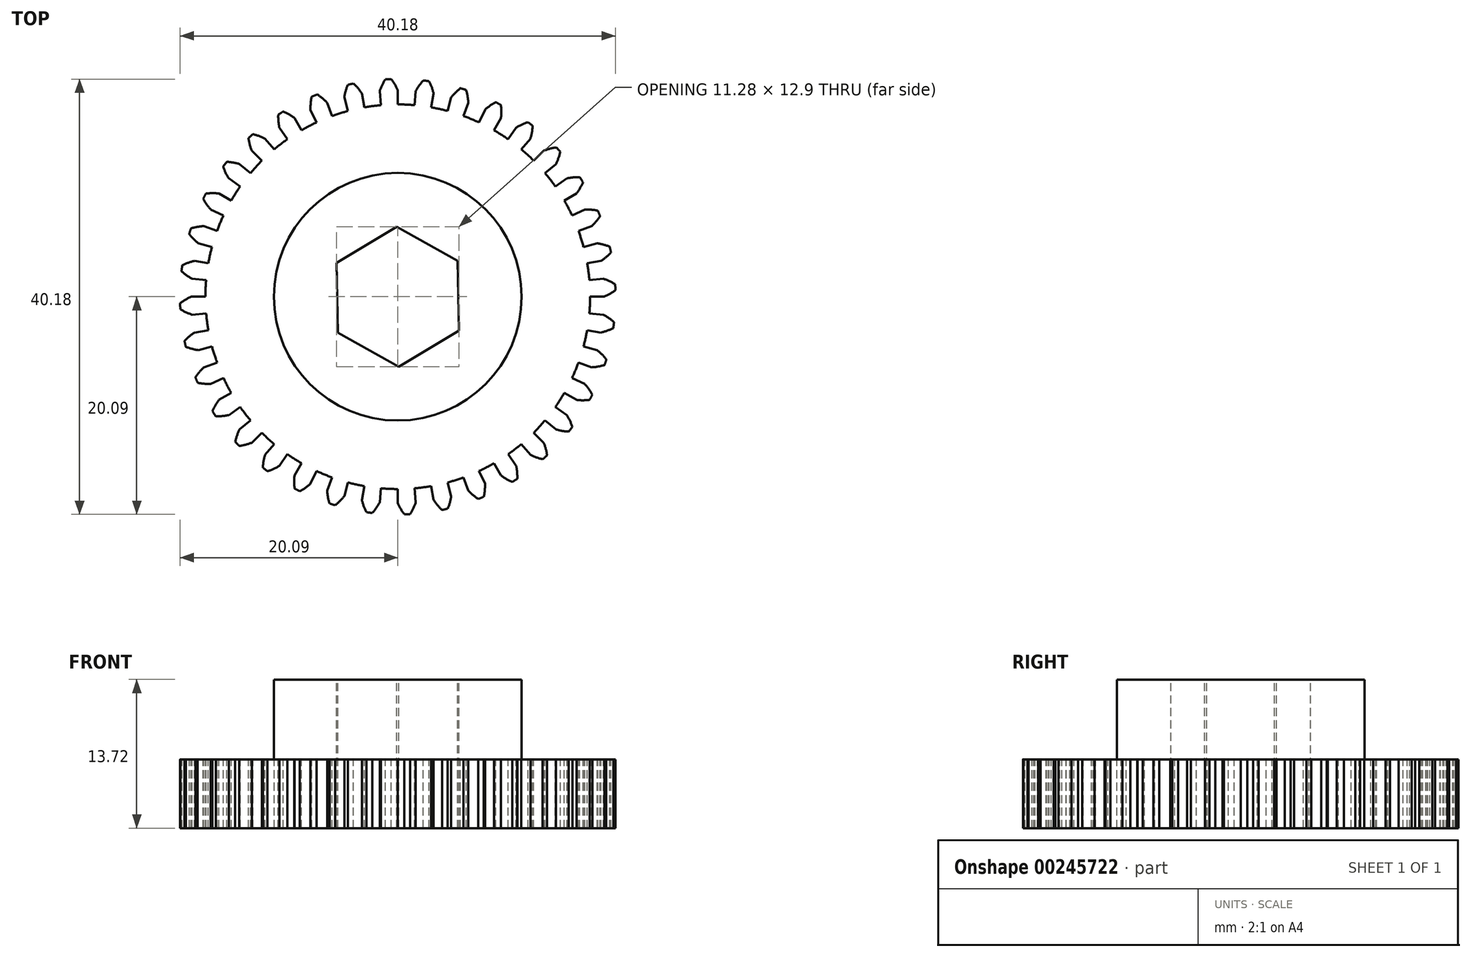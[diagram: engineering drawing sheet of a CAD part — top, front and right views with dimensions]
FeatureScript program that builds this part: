
annotation { "Feature Type Name" : "Feature", "Feature Type Description" : "" }
export const myFeature = defineFeature(function(context is Context, id is Id, definition is map)
    precondition{}
    {
        {
            var Q0;
            Q0=qCreatedBy(makeId("Top.planeOp"),FACE);
            var sketch = newSketch(context, id + "F0", { "sketchPlane" : qUnion([Q0])});
            skArc(sketch, "E0", {"start": v(-0.6, 20.1) * mm, "mid": v(-0.74, 20.1) * mm, "end": v(-0.88, 20.08) * mm});
            skLineSegment(sketch, "E1", {"start": v(0, 17.75) * mm, "end": v(0, 19.05) * mm});
            skLineSegment(sketch, "E2", {"start": v(-1.55, 17.69) * mm, "end": v(-1.66, 18.98) * mm});
            skArc(sketch, "E3", {"start": v(-4.6, 17.15) * mm, "mid": v(-5.34, 16.93) * mm, "end": v(-6.07, 16.68) * mm});
            skArc(sketch, "E4", {"start": v(0, 19.05) * mm, "mid": v(-0.27, 19.6) * mm, "end": v(-0.6, 20.1) * mm});
            skArc(sketch, "E5.MirrorCS", {"start": v(-1.66, 18.98) * mm, "mid": v(-1.44, 19.54) * mm, "end": v(-1.15, 20.07) * mm});
            skArc(sketch, "E6.MirrorCS", {"start": v(-1.15, 20.07) * mm, "mid": v(-1.01, 20.08) * mm, "end": v(-0.88, 20.08) * mm});
            skLineSegment(sketch, "E7.1.0", {"start": v(-4.6, 17.15) * mm, "end": v(-4.93, 18.4) * mm});
            skArc(sketch, "E7.1.1", {"start": v(-4.93, 18.4) * mm, "mid": v(-4.81, 19) * mm, "end": v(-4.62, 19.57) * mm});
            skArc(sketch, "E7.1.2", {"start": v(-4.62, 19.57) * mm, "mid": v(-4.48, 19.6) * mm, "end": v(-4.35, 19.63) * mm});
            skArc(sketch, "E7.1.3", {"start": v(-4.09, 19.68) * mm, "mid": v(-4.22, 19.66) * mm, "end": v(-4.35, 19.63) * mm});
            skArc(sketch, "E7.1.4", {"start": v(-3.3, 18.76) * mm, "mid": v(-3.67, 19.25) * mm, "end": v(-4.09, 19.68) * mm});
            skLineSegment(sketch, "E7.1.5", {"start": v(-3.08, 17.49) * mm, "end": v(-3.3, 18.76) * mm});
            skLineSegment(sketch, "E7.2.0", {"start": v(-7.5, 16.1) * mm, "end": v(-8.05, 17.27) * mm});
            skArc(sketch, "E7.2.1", {"start": v(-8.05, 17.27) * mm, "mid": v(-8.04, 17.87) * mm, "end": v(-7.94, 18.47) * mm});
            skArc(sketch, "E7.2.2", {"start": v(-7.94, 18.47) * mm, "mid": v(-7.82, 18.52) * mm, "end": v(-7.7, 18.57) * mm});
            skArc(sketch, "E7.2.3", {"start": v(-7.44, 18.68) * mm, "mid": v(-7.57, 18.63) * mm, "end": v(-7.7, 18.57) * mm});
            skArc(sketch, "E7.2.4", {"start": v(-6.52, 17.9) * mm, "mid": v(-6.95, 18.32) * mm, "end": v(-7.44, 18.68) * mm});
            skLineSegment(sketch, "E7.2.5", {"start": v(-6.07, 16.68) * mm, "end": v(-6.52, 17.9) * mm});
            skLineSegment(sketch, "E7.3.0", {"start": v(-10.18, 14.54) * mm, "end": v(-10.93, 15.6) * mm});
            skArc(sketch, "E7.3.1", {"start": v(-10.93, 15.6) * mm, "mid": v(-11.02, 16.2) * mm, "end": v(-11.03, 16.8) * mm});
            skArc(sketch, "E7.3.2", {"start": v(-11.03, 16.8) * mm, "mid": v(-10.92, 16.88) * mm, "end": v(-10.8, 16.96) * mm});
            skArc(sketch, "E7.3.3", {"start": v(-10.57, 17.1) * mm, "mid": v(-10.69, 17.03) * mm, "end": v(-10.8, 16.96) * mm});
            skArc(sketch, "E7.3.4", {"start": v(-9.53, 16.5) * mm, "mid": v(-10.03, 16.83) * mm, "end": v(-10.57, 17.1) * mm});
            skLineSegment(sketch, "E7.3.5", {"start": v(-8.88, 15.38) * mm, "end": v(-9.52, 16.5) * mm});
            skLineSegment(sketch, "E7.4.0", {"start": v(-12.55, 12.55) * mm, "end": v(-13.47, 13.47) * mm});
            skArc(sketch, "E7.4.1", {"start": v(-13.47, 13.47) * mm, "mid": v(-13.66, 14.04) * mm, "end": v(-13.78, 14.64) * mm});
            skArc(sketch, "E7.4.2", {"start": v(-13.78, 14.64) * mm, "mid": v(-13.68, 14.73) * mm, "end": v(-13.58, 14.82) * mm});
            skArc(sketch, "E7.4.3", {"start": v(-13.38, 15) * mm, "mid": v(-13.48, 14.91) * mm, "end": v(-13.58, 14.82) * mm});
            skArc(sketch, "E7.4.4", {"start": v(-12.25, 14.6) * mm, "mid": v(-12.8, 14.83) * mm, "end": v(-13.38, 15) * mm});
            skLineSegment(sketch, "E7.4.5", {"start": v(-11.41, 13.6) * mm, "end": v(-12.25, 14.6) * mm});
            skLineSegment(sketch, "E7.5.0", {"start": v(-14.54, 10.18) * mm, "end": v(-15.6, 10.93) * mm});
            skArc(sketch, "E7.5.1", {"start": v(-15.6, 10.93) * mm, "mid": v(-15.9, 11.46) * mm, "end": v(-16.11, 12.02) * mm});
            skArc(sketch, "E7.5.2", {"start": v(-16.11, 12.02) * mm, "mid": v(-16.03, 12.13) * mm, "end": v(-15.95, 12.24) * mm});
            skArc(sketch, "E7.5.3", {"start": v(-15.78, 12.45) * mm, "mid": v(-15.87, 12.35) * mm, "end": v(-15.95, 12.24) * mm});
            skArc(sketch, "E7.5.4", {"start": v(-14.6, 12.25) * mm, "mid": v(-15.18, 12.39) * mm, "end": v(-15.78, 12.45) * mm});
            skLineSegment(sketch, "E7.5.5", {"start": v(-13.6, 11.41) * mm, "end": v(-14.6, 12.25) * mm});
            skLineSegment(sketch, "E7.6.0", {"start": v(-16.1, 7.5) * mm, "end": v(-17.27, 8.05) * mm});
            skArc(sketch, "E7.6.1", {"start": v(-17.27, 8.05) * mm, "mid": v(-17.64, 8.52) * mm, "end": v(-17.96, 9.04) * mm});
            skArc(sketch, "E7.6.2", {"start": v(-17.96, 9.04) * mm, "mid": v(-17.9, 9.16) * mm, "end": v(-17.83, 9.28) * mm});
            skArc(sketch, "E7.6.3", {"start": v(-17.7, 9.52) * mm, "mid": v(-17.77, 9.4) * mm, "end": v(-17.83, 9.28) * mm});
            skArc(sketch, "E7.6.4", {"start": v(-16.5, 9.53) * mm, "mid": v(-17.1, 9.56) * mm, "end": v(-17.7, 9.52) * mm});
            skLineSegment(sketch, "E7.6.5", {"start": v(-15.38, 8.88) * mm, "end": v(-16.5, 9.53) * mm});
            skLineSegment(sketch, "E7.7.0", {"start": v(-17.15, 4.6) * mm, "end": v(-18.4, 4.93) * mm});
            skArc(sketch, "E7.7.1", {"start": v(-18.4, 4.93) * mm, "mid": v(-18.85, 5.33) * mm, "end": v(-19.25, 5.79) * mm});
            skArc(sketch, "E7.7.2", {"start": v(-19.25, 5.79) * mm, "mid": v(-19.21, 5.92) * mm, "end": v(-19.17, 6.05) * mm});
            skArc(sketch, "E7.7.3", {"start": v(-19.1, 6.3) * mm, "mid": v(-19.13, 6.17) * mm, "end": v(-19.17, 6.05) * mm});
            skArc(sketch, "E7.7.4", {"start": v(-17.9, 6.52) * mm, "mid": v(-18.5, 6.45) * mm, "end": v(-19.1, 6.3) * mm});
            skLineSegment(sketch, "E7.7.5", {"start": v(-16.68, 6.07) * mm, "end": v(-17.9, 6.52) * mm});
            skLineSegment(sketch, "E7.8.0", {"start": v(-17.69, 1.55) * mm, "end": v(-18.98, 1.66) * mm});
            skArc(sketch, "E7.8.1", {"start": v(-18.98, 1.66) * mm, "mid": v(-19.5, 1.98) * mm, "end": v(-19.97, 2.35) * mm});
            skArc(sketch, "E7.8.2", {"start": v(-19.97, 2.35) * mm, "mid": v(-19.95, 2.49) * mm, "end": v(-19.93, 2.62) * mm});
            skArc(sketch, "E7.8.3", {"start": v(-19.9, 2.9) * mm, "mid": v(-19.91, 2.76) * mm, "end": v(-19.93, 2.62) * mm});
            skArc(sketch, "E7.8.4", {"start": v(-18.76, 3.3) * mm, "mid": v(-19.34, 3.14) * mm, "end": v(-19.9, 2.9) * mm});
            skLineSegment(sketch, "E7.8.5", {"start": v(-17.49, 3.08) * mm, "end": v(-18.76, 3.3) * mm});
            skLineSegment(sketch, "E7.9.0", {"start": v(-17.69, -1.55) * mm, "end": v(-18.98, -1.66) * mm});
            skArc(sketch, "E7.9.1", {"start": v(-18.98, -1.66) * mm, "mid": v(-19.54, -1.44) * mm, "end": v(-20.07, -1.15) * mm});
            skArc(sketch, "E7.9.2", {"start": v(-20.07, -1.15) * mm, "mid": v(-20.08, -1.01) * mm, "end": v(-20.08, -0.88) * mm});
            skArc(sketch, "E7.9.3", {"start": v(-20.1, -0.6) * mm, "mid": v(-20.1, -0.74) * mm, "end": v(-20.08, -0.88) * mm});
            skArc(sketch, "E7.9.4", {"start": v(-19.05, 0) * mm, "mid": v(-19.6, -0.27) * mm, "end": v(-20.1, -0.6) * mm});
            skLineSegment(sketch, "E7.9.5", {"start": v(-17.75, 0) * mm, "end": v(-19.05, 0) * mm});
            skLineSegment(sketch, "E7.10.0", {"start": v(-17.15, -4.6) * mm, "end": v(-18.4, -4.93) * mm});
            skArc(sketch, "E7.10.1", {"start": v(-18.4, -4.93) * mm, "mid": v(-19, -4.81) * mm, "end": v(-19.57, -4.62) * mm});
            skArc(sketch, "E7.10.2", {"start": v(-19.57, -4.62) * mm, "mid": v(-19.6, -4.48) * mm, "end": v(-19.63, -4.35) * mm});
            skArc(sketch, "E7.10.3", {"start": v(-19.68, -4.09) * mm, "mid": v(-19.66, -4.22) * mm, "end": v(-19.63, -4.35) * mm});
            skArc(sketch, "E7.10.4", {"start": v(-18.76, -3.3) * mm, "mid": v(-19.25, -3.67) * mm, "end": v(-19.68, -4.09) * mm});
            skLineSegment(sketch, "E7.10.5", {"start": v(-17.49, -3.08) * mm, "end": v(-18.76, -3.3) * mm});
            skLineSegment(sketch, "E7.11.0", {"start": v(-16.1, -7.5) * mm, "end": v(-17.27, -8.05) * mm});
            skArc(sketch, "E7.11.1", {"start": v(-17.27, -8.05) * mm, "mid": v(-17.87, -8.04) * mm, "end": v(-18.47, -7.94) * mm});
            skArc(sketch, "E7.11.2", {"start": v(-18.47, -7.94) * mm, "mid": v(-18.52, -7.82) * mm, "end": v(-18.57, -7.7) * mm});
            skArc(sketch, "E7.11.3", {"start": v(-18.68, -7.44) * mm, "mid": v(-18.63, -7.57) * mm, "end": v(-18.57, -7.7) * mm});
            skArc(sketch, "E7.11.4", {"start": v(-17.9, -6.52) * mm, "mid": v(-18.32, -6.95) * mm, "end": v(-18.68, -7.44) * mm});
            skLineSegment(sketch, "E7.11.5", {"start": v(-16.68, -6.07) * mm, "end": v(-17.9, -6.52) * mm});
            skLineSegment(sketch, "E7.12.0", {"start": v(-14.54, -10.18) * mm, "end": v(-15.6, -10.93) * mm});
            skArc(sketch, "E7.12.1", {"start": v(-15.6, -10.93) * mm, "mid": v(-16.2, -11.02) * mm, "end": v(-16.8, -11.03) * mm});
            skArc(sketch, "E7.12.2", {"start": v(-16.8, -11.03) * mm, "mid": v(-16.88, -10.92) * mm, "end": v(-16.96, -10.8) * mm});
            skArc(sketch, "E7.12.3", {"start": v(-17.1, -10.57) * mm, "mid": v(-17.03, -10.69) * mm, "end": v(-16.96, -10.8) * mm});
            skArc(sketch, "E7.12.4", {"start": v(-16.5, -9.52) * mm, "mid": v(-16.83, -10.03) * mm, "end": v(-17.1, -10.57) * mm});
            skLineSegment(sketch, "E7.12.5", {"start": v(-15.38, -8.88) * mm, "end": v(-16.5, -9.52) * mm});
            skLineSegment(sketch, "E7.13.0", {"start": v(-12.55, -12.55) * mm, "end": v(-13.47, -13.47) * mm});
            skArc(sketch, "E7.13.1", {"start": v(-13.47, -13.47) * mm, "mid": v(-14.04, -13.66) * mm, "end": v(-14.64, -13.78) * mm});
            skArc(sketch, "E7.13.2", {"start": v(-14.64, -13.78) * mm, "mid": v(-14.73, -13.68) * mm, "end": v(-14.82, -13.58) * mm});
            skArc(sketch, "E7.13.3", {"start": v(-15, -13.38) * mm, "mid": v(-14.91, -13.48) * mm, "end": v(-14.82, -13.58) * mm});
            skArc(sketch, "E7.13.4", {"start": v(-14.6, -12.25) * mm, "mid": v(-14.83, -12.8) * mm, "end": v(-15, -13.38) * mm});
            skLineSegment(sketch, "E7.13.5", {"start": v(-13.6, -11.41) * mm, "end": v(-14.6, -12.25) * mm});
            skLineSegment(sketch, "E7.14.0", {"start": v(-10.18, -14.54) * mm, "end": v(-10.93, -15.6) * mm});
            skArc(sketch, "E7.14.1", {"start": v(-10.93, -15.6) * mm, "mid": v(-11.46, -15.9) * mm, "end": v(-12.02, -16.11) * mm});
            skArc(sketch, "E7.14.2", {"start": v(-12.02, -16.11) * mm, "mid": v(-12.13, -16.03) * mm, "end": v(-12.24, -15.95) * mm});
            skArc(sketch, "E7.14.3", {"start": v(-12.45, -15.78) * mm, "mid": v(-12.35, -15.87) * mm, "end": v(-12.24, -15.95) * mm});
            skArc(sketch, "E7.14.4", {"start": v(-12.25, -14.6) * mm, "mid": v(-12.39, -15.18) * mm, "end": v(-12.45, -15.78) * mm});
            skLineSegment(sketch, "E7.14.5", {"start": v(-11.41, -13.6) * mm, "end": v(-12.25, -14.6) * mm});
            skLineSegment(sketch, "E7.15.0", {"start": v(-7.5, -16.1) * mm, "end": v(-8.05, -17.27) * mm});
            skArc(sketch, "E7.15.1", {"start": v(-8.05, -17.27) * mm, "mid": v(-8.52, -17.64) * mm, "end": v(-9.04, -17.96) * mm});
            skArc(sketch, "E7.15.2", {"start": v(-9.04, -17.96) * mm, "mid": v(-9.16, -17.9) * mm, "end": v(-9.28, -17.83) * mm});
            skArc(sketch, "E7.15.3", {"start": v(-9.52, -17.7) * mm, "mid": v(-9.4, -17.77) * mm, "end": v(-9.28, -17.83) * mm});
            skArc(sketch, "E7.15.4", {"start": v(-9.53, -16.5) * mm, "mid": v(-9.56, -17.1) * mm, "end": v(-9.52, -17.7) * mm});
            skLineSegment(sketch, "E7.15.5", {"start": v(-8.88, -15.38) * mm, "end": v(-9.53, -16.5) * mm});
            skLineSegment(sketch, "E7.16.0", {"start": v(-4.6, -17.15) * mm, "end": v(-4.93, -18.4) * mm});
            skArc(sketch, "E7.16.1", {"start": v(-4.93, -18.4) * mm, "mid": v(-5.33, -18.85) * mm, "end": v(-5.79, -19.25) * mm});
            skArc(sketch, "E7.16.2", {"start": v(-5.79, -19.25) * mm, "mid": v(-5.92, -19.21) * mm, "end": v(-6.05, -19.17) * mm});
            skArc(sketch, "E7.16.3", {"start": v(-6.3, -19.1) * mm, "mid": v(-6.17, -19.13) * mm, "end": v(-6.05, -19.17) * mm});
            skArc(sketch, "E7.16.4", {"start": v(-6.52, -17.9) * mm, "mid": v(-6.45, -18.5) * mm, "end": v(-6.3, -19.1) * mm});
            skLineSegment(sketch, "E7.16.5", {"start": v(-6.07, -16.68) * mm, "end": v(-6.52, -17.9) * mm});
            skLineSegment(sketch, "E7.17.0", {"start": v(-1.55, -17.69) * mm, "end": v(-1.66, -18.98) * mm});
            skArc(sketch, "E7.17.1", {"start": v(-1.66, -18.98) * mm, "mid": v(-1.98, -19.5) * mm, "end": v(-2.35, -19.97) * mm});
            skArc(sketch, "E7.17.2", {"start": v(-2.35, -19.97) * mm, "mid": v(-2.49, -19.95) * mm, "end": v(-2.62, -19.93) * mm});
            skArc(sketch, "E7.17.3", {"start": v(-2.9, -19.9) * mm, "mid": v(-2.76, -19.91) * mm, "end": v(-2.62, -19.93) * mm});
            skArc(sketch, "E7.17.4", {"start": v(-3.3, -18.76) * mm, "mid": v(-3.14, -19.34) * mm, "end": v(-2.9, -19.9) * mm});
            skLineSegment(sketch, "E7.17.5", {"start": v(-3.08, -17.49) * mm, "end": v(-3.3, -18.76) * mm});
            skLineSegment(sketch, "E7.18.0", {"start": v(1.55, -17.69) * mm, "end": v(1.66, -18.98) * mm});
            skArc(sketch, "E7.18.1", {"start": v(1.66, -18.98) * mm, "mid": v(1.44, -19.54) * mm, "end": v(1.15, -20.07) * mm});
            skArc(sketch, "E7.18.2", {"start": v(1.15, -20.07) * mm, "mid": v(1.01, -20.08) * mm, "end": v(0.88, -20.08) * mm});
            skArc(sketch, "E7.18.3", {"start": v(0.6, -20.1) * mm, "mid": v(0.74, -20.1) * mm, "end": v(0.88, -20.08) * mm});
            skArc(sketch, "E7.18.4", {"start": v(0, -19.05) * mm, "mid": v(0.27, -19.6) * mm, "end": v(0.6, -20.1) * mm});
            skLineSegment(sketch, "E7.18.5", {"start": v(0, -17.75) * mm, "end": v(0, -19.05) * mm});
            skLineSegment(sketch, "E7.19.0", {"start": v(4.6, -17.15) * mm, "end": v(4.93, -18.4) * mm});
            skArc(sketch, "E7.19.1", {"start": v(4.93, -18.4) * mm, "mid": v(4.81, -19) * mm, "end": v(4.62, -19.57) * mm});
            skArc(sketch, "E7.19.2", {"start": v(4.62, -19.57) * mm, "mid": v(4.48, -19.6) * mm, "end": v(4.35, -19.63) * mm});
            skArc(sketch, "E7.19.3", {"start": v(4.09, -19.68) * mm, "mid": v(4.22, -19.66) * mm, "end": v(4.35, -19.63) * mm});
            skArc(sketch, "E7.19.4", {"start": v(3.3, -18.76) * mm, "mid": v(3.67, -19.25) * mm, "end": v(4.09, -19.68) * mm});
            skLineSegment(sketch, "E7.19.5", {"start": v(3.08, -17.49) * mm, "end": v(3.3, -18.76) * mm});
            skLineSegment(sketch, "E7.20.0", {"start": v(7.5, -16.1) * mm, "end": v(8.05, -17.27) * mm});
            skArc(sketch, "E7.20.1", {"start": v(8.05, -17.27) * mm, "mid": v(8.04, -17.87) * mm, "end": v(7.94, -18.47) * mm});
            skArc(sketch, "E7.20.2", {"start": v(7.94, -18.47) * mm, "mid": v(7.82, -18.52) * mm, "end": v(7.7, -18.57) * mm});
            skArc(sketch, "E7.20.3", {"start": v(7.44, -18.68) * mm, "mid": v(7.57, -18.63) * mm, "end": v(7.7, -18.57) * mm});
            skArc(sketch, "E7.20.4", {"start": v(6.52, -17.9) * mm, "mid": v(6.95, -18.32) * mm, "end": v(7.44, -18.68) * mm});
            skLineSegment(sketch, "E7.20.5", {"start": v(6.07, -16.68) * mm, "end": v(6.52, -17.9) * mm});
            skLineSegment(sketch, "E7.21.0", {"start": v(10.18, -14.54) * mm, "end": v(10.93, -15.6) * mm});
            skArc(sketch, "E7.21.1", {"start": v(10.93, -15.6) * mm, "mid": v(11.02, -16.2) * mm, "end": v(11.03, -16.8) * mm});
            skArc(sketch, "E7.21.2", {"start": v(11.03, -16.8) * mm, "mid": v(10.92, -16.88) * mm, "end": v(10.8, -16.96) * mm});
            skArc(sketch, "E7.21.3", {"start": v(10.57, -17.1) * mm, "mid": v(10.69, -17.03) * mm, "end": v(10.8, -16.96) * mm});
            skArc(sketch, "E7.21.4", {"start": v(9.53, -16.5) * mm, "mid": v(10.03, -16.83) * mm, "end": v(10.57, -17.1) * mm});
            skLineSegment(sketch, "E7.21.5", {"start": v(8.88, -15.38) * mm, "end": v(9.53, -16.5) * mm});
            skLineSegment(sketch, "E7.22.0", {"start": v(12.55, -12.55) * mm, "end": v(13.47, -13.47) * mm});
            skArc(sketch, "E7.22.1", {"start": v(13.47, -13.47) * mm, "mid": v(13.66, -14.04) * mm, "end": v(13.78, -14.64) * mm});
            skArc(sketch, "E7.22.2", {"start": v(13.78, -14.64) * mm, "mid": v(13.68, -14.73) * mm, "end": v(13.58, -14.82) * mm});
            skArc(sketch, "E7.22.3", {"start": v(13.38, -15) * mm, "mid": v(13.48, -14.91) * mm, "end": v(13.58, -14.82) * mm});
            skArc(sketch, "E7.22.4", {"start": v(12.25, -14.6) * mm, "mid": v(12.8, -14.83) * mm, "end": v(13.38, -15) * mm});
            skLineSegment(sketch, "E7.22.5", {"start": v(11.41, -13.6) * mm, "end": v(12.25, -14.6) * mm});
            skLineSegment(sketch, "E7.23.0", {"start": v(14.54, -10.18) * mm, "end": v(15.6, -10.93) * mm});
            skArc(sketch, "E7.23.1", {"start": v(15.6, -10.93) * mm, "mid": v(15.9, -11.46) * mm, "end": v(16.11, -12.02) * mm});
            skArc(sketch, "E7.23.2", {"start": v(16.11, -12.02) * mm, "mid": v(16.03, -12.13) * mm, "end": v(15.95, -12.24) * mm});
            skArc(sketch, "E7.23.3", {"start": v(15.78, -12.45) * mm, "mid": v(15.87, -12.35) * mm, "end": v(15.95, -12.24) * mm});
            skArc(sketch, "E7.23.4", {"start": v(14.6, -12.25) * mm, "mid": v(15.18, -12.39) * mm, "end": v(15.78, -12.45) * mm});
            skLineSegment(sketch, "E7.23.5", {"start": v(13.6, -11.41) * mm, "end": v(14.6, -12.25) * mm});
            skLineSegment(sketch, "E7.24.0", {"start": v(16.1, -7.5) * mm, "end": v(17.27, -8.05) * mm});
            skArc(sketch, "E7.24.1", {"start": v(17.27, -8.05) * mm, "mid": v(17.64, -8.52) * mm, "end": v(17.96, -9.04) * mm});
            skArc(sketch, "E7.24.2", {"start": v(17.96, -9.04) * mm, "mid": v(17.9, -9.16) * mm, "end": v(17.83, -9.28) * mm});
            skArc(sketch, "E7.24.3", {"start": v(17.7, -9.52) * mm, "mid": v(17.77, -9.4) * mm, "end": v(17.83, -9.28) * mm});
            skArc(sketch, "E7.24.4", {"start": v(16.5, -9.53) * mm, "mid": v(17.1, -9.56) * mm, "end": v(17.7, -9.52) * mm});
            skLineSegment(sketch, "E7.24.5", {"start": v(15.38, -8.88) * mm, "end": v(16.5, -9.53) * mm});
            skLineSegment(sketch, "E7.25.0", {"start": v(17.15, -4.6) * mm, "end": v(18.4, -4.93) * mm});
            skArc(sketch, "E7.25.1", {"start": v(18.4, -4.93) * mm, "mid": v(18.85, -5.33) * mm, "end": v(19.25, -5.79) * mm});
            skArc(sketch, "E7.25.2", {"start": v(19.25, -5.79) * mm, "mid": v(19.21, -5.92) * mm, "end": v(19.17, -6.05) * mm});
            skArc(sketch, "E7.25.3", {"start": v(19.1, -6.3) * mm, "mid": v(19.13, -6.17) * mm, "end": v(19.17, -6.05) * mm});
            skArc(sketch, "E7.25.4", {"start": v(17.9, -6.52) * mm, "mid": v(18.5, -6.45) * mm, "end": v(19.1, -6.3) * mm});
            skLineSegment(sketch, "E7.25.5", {"start": v(16.68, -6.07) * mm, "end": v(17.9, -6.52) * mm});
            skLineSegment(sketch, "E7.26.0", {"start": v(17.69, -1.55) * mm, "end": v(18.98, -1.66) * mm});
            skArc(sketch, "E7.26.1", {"start": v(18.98, -1.66) * mm, "mid": v(19.5, -1.98) * mm, "end": v(19.97, -2.35) * mm});
            skArc(sketch, "E7.26.2", {"start": v(19.97, -2.35) * mm, "mid": v(19.95, -2.49) * mm, "end": v(19.93, -2.62) * mm});
            skArc(sketch, "E7.26.3", {"start": v(19.9, -2.9) * mm, "mid": v(19.91, -2.76) * mm, "end": v(19.93, -2.62) * mm});
            skArc(sketch, "E7.26.4", {"start": v(18.76, -3.3) * mm, "mid": v(19.34, -3.14) * mm, "end": v(19.9, -2.9) * mm});
            skLineSegment(sketch, "E7.26.5", {"start": v(17.49, -3.08) * mm, "end": v(18.76, -3.3) * mm});
            skLineSegment(sketch, "E7.27.0", {"start": v(17.69, 1.55) * mm, "end": v(18.98, 1.66) * mm});
            skArc(sketch, "E7.27.1", {"start": v(18.98, 1.66) * mm, "mid": v(19.54, 1.44) * mm, "end": v(20.07, 1.15) * mm});
            skArc(sketch, "E7.27.2", {"start": v(20.07, 1.15) * mm, "mid": v(20.08, 1.01) * mm, "end": v(20.08, 0.88) * mm});
            skArc(sketch, "E7.27.3", {"start": v(20.1, 0.6) * mm, "mid": v(20.1, 0.74) * mm, "end": v(20.08, 0.88) * mm});
            skArc(sketch, "E7.27.4", {"start": v(19.05, 0) * mm, "mid": v(19.6, 0.27) * mm, "end": v(20.1, 0.6) * mm});
            skLineSegment(sketch, "E7.27.5", {"start": v(17.75, 0) * mm, "end": v(19.05, 0) * mm});
            skLineSegment(sketch, "E7.28.0", {"start": v(17.15, 4.6) * mm, "end": v(18.4, 4.93) * mm});
            skArc(sketch, "E7.28.1", {"start": v(18.4, 4.93) * mm, "mid": v(19, 4.81) * mm, "end": v(19.57, 4.62) * mm});
            skArc(sketch, "E7.28.2", {"start": v(19.57, 4.62) * mm, "mid": v(19.6, 4.48) * mm, "end": v(19.63, 4.35) * mm});
            skArc(sketch, "E7.28.3", {"start": v(19.68, 4.09) * mm, "mid": v(19.66, 4.22) * mm, "end": v(19.63, 4.35) * mm});
            skArc(sketch, "E7.28.4", {"start": v(18.76, 3.3) * mm, "mid": v(19.25, 3.67) * mm, "end": v(19.68, 4.09) * mm});
            skLineSegment(sketch, "E7.28.5", {"start": v(17.49, 3.08) * mm, "end": v(18.76, 3.3) * mm});
            skLineSegment(sketch, "E7.29.0", {"start": v(16.1, 7.5) * mm, "end": v(17.27, 8.05) * mm});
            skArc(sketch, "E7.29.1", {"start": v(17.27, 8.05) * mm, "mid": v(17.87, 8.04) * mm, "end": v(18.47, 7.94) * mm});
            skArc(sketch, "E7.29.2", {"start": v(18.47, 7.94) * mm, "mid": v(18.52, 7.82) * mm, "end": v(18.57, 7.7) * mm});
            skArc(sketch, "E7.29.3", {"start": v(18.68, 7.44) * mm, "mid": v(18.63, 7.57) * mm, "end": v(18.57, 7.7) * mm});
            skArc(sketch, "E7.29.4", {"start": v(17.9, 6.52) * mm, "mid": v(18.32, 6.95) * mm, "end": v(18.68, 7.44) * mm});
            skLineSegment(sketch, "E7.29.5", {"start": v(16.68, 6.07) * mm, "end": v(17.9, 6.52) * mm});
            skLineSegment(sketch, "E7.30.0", {"start": v(14.54, 10.18) * mm, "end": v(15.6, 10.93) * mm});
            skArc(sketch, "E7.30.1", {"start": v(15.6, 10.93) * mm, "mid": v(16.2, 11.02) * mm, "end": v(16.8, 11.03) * mm});
            skArc(sketch, "E7.30.2", {"start": v(16.8, 11.03) * mm, "mid": v(16.88, 10.92) * mm, "end": v(16.96, 10.8) * mm});
            skArc(sketch, "E7.30.3", {"start": v(17.1, 10.57) * mm, "mid": v(17.03, 10.69) * mm, "end": v(16.96, 10.8) * mm});
            skArc(sketch, "E7.30.4", {"start": v(16.5, 9.52) * mm, "mid": v(16.83, 10.03) * mm, "end": v(17.1, 10.57) * mm});
            skLineSegment(sketch, "E7.30.5", {"start": v(15.38, 8.88) * mm, "end": v(16.5, 9.52) * mm});
            skLineSegment(sketch, "E7.31.0", {"start": v(12.55, 12.55) * mm, "end": v(13.47, 13.47) * mm});
            skArc(sketch, "E7.31.1", {"start": v(13.47, 13.47) * mm, "mid": v(14.04, 13.66) * mm, "end": v(14.64, 13.78) * mm});
            skArc(sketch, "E7.31.2", {"start": v(14.64, 13.78) * mm, "mid": v(14.73, 13.68) * mm, "end": v(14.82, 13.58) * mm});
            skArc(sketch, "E7.31.3", {"start": v(15, 13.38) * mm, "mid": v(14.91, 13.48) * mm, "end": v(14.82, 13.58) * mm});
            skArc(sketch, "E7.31.4", {"start": v(14.6, 12.25) * mm, "mid": v(14.83, 12.8) * mm, "end": v(15, 13.38) * mm});
            skLineSegment(sketch, "E7.31.5", {"start": v(13.6, 11.41) * mm, "end": v(14.6, 12.25) * mm});
            skLineSegment(sketch, "E7.32.0", {"start": v(10.18, 14.54) * mm, "end": v(10.93, 15.6) * mm});
            skArc(sketch, "E7.32.1", {"start": v(10.93, 15.6) * mm, "mid": v(11.46, 15.9) * mm, "end": v(12.02, 16.11) * mm});
            skArc(sketch, "E7.32.2", {"start": v(12.02, 16.11) * mm, "mid": v(12.13, 16.03) * mm, "end": v(12.24, 15.95) * mm});
            skArc(sketch, "E7.32.3", {"start": v(12.45, 15.78) * mm, "mid": v(12.35, 15.87) * mm, "end": v(12.24, 15.95) * mm});
            skArc(sketch, "E7.32.4", {"start": v(12.25, 14.6) * mm, "mid": v(12.39, 15.18) * mm, "end": v(12.45, 15.78) * mm});
            skLineSegment(sketch, "E7.32.5", {"start": v(11.41, 13.6) * mm, "end": v(12.25, 14.6) * mm});
            skLineSegment(sketch, "E7.33.0", {"start": v(7.5, 16.1) * mm, "end": v(8.05, 17.27) * mm});
            skArc(sketch, "E7.33.1", {"start": v(8.05, 17.27) * mm, "mid": v(8.52, 17.64) * mm, "end": v(9.04, 17.96) * mm});
            skArc(sketch, "E7.33.2", {"start": v(9.04, 17.96) * mm, "mid": v(9.16, 17.9) * mm, "end": v(9.28, 17.83) * mm});
            skArc(sketch, "E7.33.3", {"start": v(9.52, 17.7) * mm, "mid": v(9.4, 17.77) * mm, "end": v(9.28, 17.83) * mm});
            skArc(sketch, "E7.33.4", {"start": v(9.52, 16.5) * mm, "mid": v(9.56, 17.1) * mm, "end": v(9.52, 17.7) * mm});
            skLineSegment(sketch, "E7.33.5", {"start": v(8.88, 15.38) * mm, "end": v(9.52, 16.5) * mm});
            skLineSegment(sketch, "E7.34.0", {"start": v(4.6, 17.15) * mm, "end": v(4.93, 18.4) * mm});
            skArc(sketch, "E7.34.1", {"start": v(4.93, 18.4) * mm, "mid": v(5.33, 18.85) * mm, "end": v(5.79, 19.25) * mm});
            skArc(sketch, "E7.34.2", {"start": v(5.79, 19.25) * mm, "mid": v(5.92, 19.21) * mm, "end": v(6.05, 19.17) * mm});
            skArc(sketch, "E7.34.3", {"start": v(6.3, 19.1) * mm, "mid": v(6.17, 19.13) * mm, "end": v(6.05, 19.17) * mm});
            skArc(sketch, "E7.34.4", {"start": v(6.52, 17.9) * mm, "mid": v(6.45, 18.5) * mm, "end": v(6.3, 19.1) * mm});
            skLineSegment(sketch, "E7.34.5", {"start": v(6.07, 16.68) * mm, "end": v(6.52, 17.9) * mm});
            skLineSegment(sketch, "E7.35.0", {"start": v(1.55, 17.69) * mm, "end": v(1.66, 18.98) * mm});
            skArc(sketch, "E7.35.1", {"start": v(1.66, 18.98) * mm, "mid": v(1.98, 19.5) * mm, "end": v(2.35, 19.97) * mm});
            skArc(sketch, "E7.35.2", {"start": v(2.35, 19.97) * mm, "mid": v(2.49, 19.95) * mm, "end": v(2.62, 19.93) * mm});
            skArc(sketch, "E7.35.3", {"start": v(2.9, 19.9) * mm, "mid": v(2.76, 19.91) * mm, "end": v(2.62, 19.93) * mm});
            skArc(sketch, "E7.35.4", {"start": v(3.3, 18.76) * mm, "mid": v(3.14, 19.34) * mm, "end": v(2.9, 19.9) * mm});
            skLineSegment(sketch, "E7.35.5", {"start": v(3.08, 17.49) * mm, "end": v(3.3, 18.76) * mm});
            skArc(sketch, "E8.trimOffspring", {"start": v(-1.55, 17.69) * mm, "mid": v(-2.32, 17.6) * mm, "end": v(-3.08, 17.49) * mm});
            skArc(sketch, "E9.trimOffspring", {"start": v(1.55, 17.69) * mm, "mid": v(0.77, 17.74) * mm, "end": v(0, 17.75) * mm});
            skArc(sketch, "E10.trimOffspring", {"start": v(4.6, 17.15) * mm, "mid": v(3.84, 17.33) * mm, "end": v(3.08, 17.49) * mm});
            skArc(sketch, "E11.trimOffspring", {"start": v(7.5, 16.1) * mm, "mid": v(6.8, 16.4) * mm, "end": v(6.07, 16.68) * mm});
            skArc(sketch, "E12.trimOffspring", {"start": v(10.18, 14.54) * mm, "mid": v(9.54, 14.97) * mm, "end": v(8.88, 15.38) * mm});
            skArc(sketch, "E13.trimOffspring", {"start": v(12.55, 12.55) * mm, "mid": v(12, 13.1) * mm, "end": v(11.41, 13.6) * mm});
            skArc(sketch, "E14.trimOffspring", {"start": v(14.54, 10.18) * mm, "mid": v(14.09, 10.8) * mm, "end": v(13.6, 11.41) * mm});
            skArc(sketch, "E15.trimOffspring", {"start": v(-7.5, 16.1) * mm, "mid": v(-8.2, 15.75) * mm, "end": v(-8.88, 15.38) * mm});
            skArc(sketch, "E16.trimOffspring", {"start": v(-10.18, 14.54) * mm, "mid": v(-10.8, 14.09) * mm, "end": v(-11.41, 13.6) * mm});
            skArc(sketch, "E17.trimOffspring", {"start": v(-12.55, 12.55) * mm, "mid": v(-13.1, 12) * mm, "end": v(-13.6, 11.41) * mm});
            skArc(sketch, "E18.trimOffspring", {"start": v(-14.54, 10.18) * mm, "mid": v(-14.97, 9.54) * mm, "end": v(-15.38, 8.88) * mm});
            skArc(sketch, "E19.trimOffspring", {"start": v(-16.1, 7.5) * mm, "mid": v(-16.4, 6.8) * mm, "end": v(-16.68, 6.07) * mm});
            skArc(sketch, "E20.trimOffspring", {"start": v(-17.15, 4.6) * mm, "mid": v(-17.33, 3.84) * mm, "end": v(-17.49, 3.08) * mm});
            skArc(sketch, "E21.trimOffspring", {"start": v(-17.69, 1.55) * mm, "mid": v(-17.74, 0.77) * mm, "end": v(-17.75, 0) * mm});
            skArc(sketch, "E22.trimOffspring", {"start": v(-17.69, -1.55) * mm, "mid": v(-17.6, -2.32) * mm, "end": v(-17.49, -3.08) * mm});
            skArc(sketch, "E23.trimOffspring", {"start": v(-17.15, -4.6) * mm, "mid": v(-16.93, -5.34) * mm, "end": v(-16.68, -6.07) * mm});
            skArc(sketch, "E24.trimOffspring", {"start": v(-16.1, -7.5) * mm, "mid": v(-15.75, -8.2) * mm, "end": v(-15.38, -8.88) * mm});
            skArc(sketch, "E25.trimOffspring", {"start": v(-14.54, -10.18) * mm, "mid": v(-14.09, -10.8) * mm, "end": v(-13.6, -11.41) * mm});
            skArc(sketch, "E26.trimOffspring", {"start": v(-12.55, -12.55) * mm, "mid": v(-12, -13.1) * mm, "end": v(-11.41, -13.6) * mm});
            skArc(sketch, "E27.trimOffspring", {"start": v(-10.18, -14.54) * mm, "mid": v(-9.54, -14.97) * mm, "end": v(-8.88, -15.38) * mm});
            skArc(sketch, "E28.trimOffspring", {"start": v(-7.5, -16.1) * mm, "mid": v(-6.8, -16.4) * mm, "end": v(-6.07, -16.68) * mm});
            skArc(sketch, "E29.trimOffspring", {"start": v(-4.6, -17.15) * mm, "mid": v(-3.84, -17.33) * mm, "end": v(-3.08, -17.49) * mm});
            skArc(sketch, "E30.trimOffspring", {"start": v(-1.55, -17.69) * mm, "mid": v(-0.77, -17.74) * mm, "end": v(0, -17.75) * mm});
            skArc(sketch, "E31.trimOffspring", {"start": v(1.55, -17.69) * mm, "mid": v(2.32, -17.6) * mm, "end": v(3.08, -17.49) * mm});
            skArc(sketch, "E32.trimOffspring", {"start": v(4.6, -17.15) * mm, "mid": v(5.34, -16.93) * mm, "end": v(6.07, -16.68) * mm});
            skArc(sketch, "E33.trimOffspring", {"start": v(7.5, -16.1) * mm, "mid": v(8.2, -15.75) * mm, "end": v(8.88, -15.38) * mm});
            skArc(sketch, "E34.trimOffspring", {"start": v(10.18, -14.54) * mm, "mid": v(10.8, -14.09) * mm, "end": v(11.41, -13.6) * mm});
            skArc(sketch, "E35.trimOffspring", {"start": v(12.55, -12.55) * mm, "mid": v(13.1, -12) * mm, "end": v(13.6, -11.41) * mm});
            skArc(sketch, "E36.trimOffspring", {"start": v(14.54, -10.18) * mm, "mid": v(14.97, -9.54) * mm, "end": v(15.38, -8.88) * mm});
            skArc(sketch, "E37.trimOffspring", {"start": v(16.1, -7.5) * mm, "mid": v(16.4, -6.8) * mm, "end": v(16.68, -6.07) * mm});
            skArc(sketch, "E38.trimOffspring", {"start": v(17.15, -4.6) * mm, "mid": v(17.33, -3.84) * mm, "end": v(17.49, -3.08) * mm});
            skArc(sketch, "E39.trimOffspring", {"start": v(17.69, -1.55) * mm, "mid": v(17.74, -0.77) * mm, "end": v(17.75, 0) * mm});
            skArc(sketch, "E40.trimOffspring", {"start": v(17.69, 1.55) * mm, "mid": v(17.6, 2.32) * mm, "end": v(17.49, 3.08) * mm});
            skArc(sketch, "E41.trimOffspring", {"start": v(17.15, 4.6) * mm, "mid": v(16.93, 5.34) * mm, "end": v(16.68, 6.07) * mm});
            skArc(sketch, "E42.trimOffspring", {"start": v(16.1, 7.5) * mm, "mid": v(15.75, 8.2) * mm, "end": v(15.38, 8.88) * mm});
            skSolve(sketch);
        }
        {
            var Q0;
            Q0 = qSketchRegion(id + "F0", true);
            extrude(context, id + "F1", {"entities" : qUnion([Q0]), "oppositeDirection" : true, "depth" : 6.35 * mm});
        }
        {
            var Q0;
            Q0=makeQuery(id+"F1.opExtrude","CAP_FACE",FACE,{"disambiguationData":[OSD([sQuery(id+"F0.wireOp",EDGE,"E0"),sQuery(id+"F0.wireOp",EDGE,"E1"),sQuery(id+"F0.wireOp",EDGE,"E2"),sQuery(id+"F0.wireOp",EDGE,"E3"),sQuery(id+"F0.wireOp",EDGE,"E4"),sQuery(id+"F0.wireOp",EDGE,"E5.MirrorCS"),sQuery(id+"F0.wireOp",EDGE,"E6.MirrorCS"),sQuery(id+"F0.wireOp",EDGE,"E7.1.0"),sQuery(id+"F0.wireOp",EDGE,"E7.1.1"),sQuery(id+"F0.wireOp",EDGE,"E7.1.2"),sQuery(id+"F0.wireOp",EDGE,"E7.1.3"),sQuery(id+"F0.wireOp",EDGE,"E7.1.4"),sQuery(id+"F0.wireOp",EDGE,"E7.1.5"),sQuery(id+"F0.wireOp",EDGE,"E7.2.0"),sQuery(id+"F0.wireOp",EDGE,"E7.2.1"),sQuery(id+"F0.wireOp",EDGE,"E7.2.2"),sQuery(id+"F0.wireOp",EDGE,"E7.2.3"),sQuery(id+"F0.wireOp",EDGE,"E7.2.4"),sQuery(id+"F0.wireOp",EDGE,"E7.2.5"),sQuery(id+"F0.wireOp",EDGE,"E7.3.0"),sQuery(id+"F0.wireOp",EDGE,"E7.3.1"),sQuery(id+"F0.wireOp",EDGE,"E7.3.2"),sQuery(id+"F0.wireOp",EDGE,"E7.3.3"),sQuery(id+"F0.wireOp",EDGE,"E7.3.4"),sQuery(id+"F0.wireOp",EDGE,"E7.3.5"),sQuery(id+"F0.wireOp",EDGE,"E7.4.0"),sQuery(id+"F0.wireOp",EDGE,"E7.4.1"),sQuery(id+"F0.wireOp",EDGE,"E7.4.2"),sQuery(id+"F0.wireOp",EDGE,"E7.4.3"),sQuery(id+"F0.wireOp",EDGE,"E7.4.4"),sQuery(id+"F0.wireOp",EDGE,"E7.4.5"),sQuery(id+"F0.wireOp",EDGE,"E7.5.0"),sQuery(id+"F0.wireOp",EDGE,"E7.5.1"),sQuery(id+"F0.wireOp",EDGE,"E7.5.2"),sQuery(id+"F0.wireOp",EDGE,"E7.5.3"),sQuery(id+"F0.wireOp",EDGE,"E7.5.4"),sQuery(id+"F0.wireOp",EDGE,"E7.5.5"),sQuery(id+"F0.wireOp",EDGE,"E7.6.0"),sQuery(id+"F0.wireOp",EDGE,"E7.6.1"),sQuery(id+"F0.wireOp",EDGE,"E7.6.2"),sQuery(id+"F0.wireOp",EDGE,"E7.6.3"),sQuery(id+"F0.wireOp",EDGE,"E7.6.4"),sQuery(id+"F0.wireOp",EDGE,"E7.6.5"),sQuery(id+"F0.wireOp",EDGE,"E7.7.0"),sQuery(id+"F0.wireOp",EDGE,"E7.7.1"),sQuery(id+"F0.wireOp",EDGE,"E7.7.2"),sQuery(id+"F0.wireOp",EDGE,"E7.7.3"),sQuery(id+"F0.wireOp",EDGE,"E7.7.4"),sQuery(id+"F0.wireOp",EDGE,"E7.7.5"),sQuery(id+"F0.wireOp",EDGE,"E7.8.0"),sQuery(id+"F0.wireOp",EDGE,"E7.8.1"),sQuery(id+"F0.wireOp",EDGE,"E7.8.2"),sQuery(id+"F0.wireOp",EDGE,"E7.8.3"),sQuery(id+"F0.wireOp",EDGE,"E7.8.4"),sQuery(id+"F0.wireOp",EDGE,"E7.8.5"),sQuery(id+"F0.wireOp",EDGE,"E7.9.0"),sQuery(id+"F0.wireOp",EDGE,"E7.9.1"),sQuery(id+"F0.wireOp",EDGE,"E7.9.2"),sQuery(id+"F0.wireOp",EDGE,"E7.9.3"),sQuery(id+"F0.wireOp",EDGE,"E7.9.4"),sQuery(id+"F0.wireOp",EDGE,"E7.9.5"),sQuery(id+"F0.wireOp",EDGE,"E7.10.0"),sQuery(id+"F0.wireOp",EDGE,"E7.10.1"),sQuery(id+"F0.wireOp",EDGE,"E7.10.2"),sQuery(id+"F0.wireOp",EDGE,"E7.10.3"),sQuery(id+"F0.wireOp",EDGE,"E7.10.4"),sQuery(id+"F0.wireOp",EDGE,"E7.10.5"),sQuery(id+"F0.wireOp",EDGE,"E7.11.0"),sQuery(id+"F0.wireOp",EDGE,"E7.11.1"),sQuery(id+"F0.wireOp",EDGE,"E7.11.2"),sQuery(id+"F0.wireOp",EDGE,"E7.11.3"),sQuery(id+"F0.wireOp",EDGE,"E7.11.4"),sQuery(id+"F0.wireOp",EDGE,"E7.11.5"),sQuery(id+"F0.wireOp",EDGE,"E7.12.0"),sQuery(id+"F0.wireOp",EDGE,"E7.12.1"),sQuery(id+"F0.wireOp",EDGE,"E7.12.2"),sQuery(id+"F0.wireOp",EDGE,"E7.12.3"),sQuery(id+"F0.wireOp",EDGE,"E7.12.4"),sQuery(id+"F0.wireOp",EDGE,"E7.12.5"),sQuery(id+"F0.wireOp",EDGE,"E7.13.0"),sQuery(id+"F0.wireOp",EDGE,"E7.13.1"),sQuery(id+"F0.wireOp",EDGE,"E7.13.2"),sQuery(id+"F0.wireOp",EDGE,"E7.13.3"),sQuery(id+"F0.wireOp",EDGE,"E7.13.4"),sQuery(id+"F0.wireOp",EDGE,"E7.13.5"),sQuery(id+"F0.wireOp",EDGE,"E7.14.0"),sQuery(id+"F0.wireOp",EDGE,"E7.14.1"),sQuery(id+"F0.wireOp",EDGE,"E7.14.2"),sQuery(id+"F0.wireOp",EDGE,"E7.14.3"),sQuery(id+"F0.wireOp",EDGE,"E7.14.4"),sQuery(id+"F0.wireOp",EDGE,"E7.14.5"),sQuery(id+"F0.wireOp",EDGE,"E7.15.0"),sQuery(id+"F0.wireOp",EDGE,"E7.15.1"),sQuery(id+"F0.wireOp",EDGE,"E7.15.2"),sQuery(id+"F0.wireOp",EDGE,"E7.15.3"),sQuery(id+"F0.wireOp",EDGE,"E7.15.4"),sQuery(id+"F0.wireOp",EDGE,"E7.15.5"),sQuery(id+"F0.wireOp",EDGE,"E7.16.0"),sQuery(id+"F0.wireOp",EDGE,"E7.16.1"),sQuery(id+"F0.wireOp",EDGE,"E7.16.2"),sQuery(id+"F0.wireOp",EDGE,"E7.16.3"),sQuery(id+"F0.wireOp",EDGE,"E7.16.4"),sQuery(id+"F0.wireOp",EDGE,"E7.16.5"),sQuery(id+"F0.wireOp",EDGE,"E7.17.0"),sQuery(id+"F0.wireOp",EDGE,"E7.17.1"),sQuery(id+"F0.wireOp",EDGE,"E7.17.2"),sQuery(id+"F0.wireOp",EDGE,"E7.17.3"),sQuery(id+"F0.wireOp",EDGE,"E7.17.4"),sQuery(id+"F0.wireOp",EDGE,"E7.17.5"),sQuery(id+"F0.wireOp",EDGE,"E7.18.0"),sQuery(id+"F0.wireOp",EDGE,"E7.18.1"),sQuery(id+"F0.wireOp",EDGE,"E7.18.2"),sQuery(id+"F0.wireOp",EDGE,"E7.18.3"),sQuery(id+"F0.wireOp",EDGE,"E7.18.4"),sQuery(id+"F0.wireOp",EDGE,"E7.18.5"),sQuery(id+"F0.wireOp",EDGE,"E7.19.0"),sQuery(id+"F0.wireOp",EDGE,"E7.19.1"),sQuery(id+"F0.wireOp",EDGE,"E7.19.2"),sQuery(id+"F0.wireOp",EDGE,"E7.19.3"),sQuery(id+"F0.wireOp",EDGE,"E7.19.4"),sQuery(id+"F0.wireOp",EDGE,"E7.19.5"),sQuery(id+"F0.wireOp",EDGE,"E7.20.0"),sQuery(id+"F0.wireOp",EDGE,"E7.20.1"),sQuery(id+"F0.wireOp",EDGE,"E7.20.2"),sQuery(id+"F0.wireOp",EDGE,"E7.20.3"),sQuery(id+"F0.wireOp",EDGE,"E7.20.4"),sQuery(id+"F0.wireOp",EDGE,"E7.20.5"),sQuery(id+"F0.wireOp",EDGE,"E7.21.0"),sQuery(id+"F0.wireOp",EDGE,"E7.21.1"),sQuery(id+"F0.wireOp",EDGE,"E7.21.2"),sQuery(id+"F0.wireOp",EDGE,"E7.21.3"),sQuery(id+"F0.wireOp",EDGE,"E7.21.4"),sQuery(id+"F0.wireOp",EDGE,"E7.21.5"),sQuery(id+"F0.wireOp",EDGE,"E7.22.0"),sQuery(id+"F0.wireOp",EDGE,"E7.22.1"),sQuery(id+"F0.wireOp",EDGE,"E7.22.2"),sQuery(id+"F0.wireOp",EDGE,"E7.22.3"),sQuery(id+"F0.wireOp",EDGE,"E7.22.4"),sQuery(id+"F0.wireOp",EDGE,"E7.22.5"),sQuery(id+"F0.wireOp",EDGE,"E7.23.0"),sQuery(id+"F0.wireOp",EDGE,"E7.23.1"),sQuery(id+"F0.wireOp",EDGE,"E7.23.2"),sQuery(id+"F0.wireOp",EDGE,"E7.23.3"),sQuery(id+"F0.wireOp",EDGE,"E7.23.4"),sQuery(id+"F0.wireOp",EDGE,"E7.23.5"),sQuery(id+"F0.wireOp",EDGE,"E7.24.0"),sQuery(id+"F0.wireOp",EDGE,"E7.24.1"),sQuery(id+"F0.wireOp",EDGE,"E7.24.2"),sQuery(id+"F0.wireOp",EDGE,"E7.24.3"),sQuery(id+"F0.wireOp",EDGE,"E7.24.4"),sQuery(id+"F0.wireOp",EDGE,"E7.24.5"),sQuery(id+"F0.wireOp",EDGE,"E7.25.0"),sQuery(id+"F0.wireOp",EDGE,"E7.25.1"),sQuery(id+"F0.wireOp",EDGE,"E7.25.2"),sQuery(id+"F0.wireOp",EDGE,"E7.25.3"),sQuery(id+"F0.wireOp",EDGE,"E7.25.4"),sQuery(id+"F0.wireOp",EDGE,"E7.25.5"),sQuery(id+"F0.wireOp",EDGE,"E7.26.0"),sQuery(id+"F0.wireOp",EDGE,"E7.26.1"),sQuery(id+"F0.wireOp",EDGE,"E7.26.2"),sQuery(id+"F0.wireOp",EDGE,"E7.26.3"),sQuery(id+"F0.wireOp",EDGE,"E7.26.4"),sQuery(id+"F0.wireOp",EDGE,"E7.26.5"),sQuery(id+"F0.wireOp",EDGE,"E7.27.0"),sQuery(id+"F0.wireOp",EDGE,"E7.27.1"),sQuery(id+"F0.wireOp",EDGE,"E7.27.2"),sQuery(id+"F0.wireOp",EDGE,"E7.27.3"),sQuery(id+"F0.wireOp",EDGE,"E7.27.4"),sQuery(id+"F0.wireOp",EDGE,"E7.27.5"),sQuery(id+"F0.wireOp",EDGE,"E7.28.0"),sQuery(id+"F0.wireOp",EDGE,"E7.28.1"),sQuery(id+"F0.wireOp",EDGE,"E7.28.2"),sQuery(id+"F0.wireOp",EDGE,"E7.28.3"),sQuery(id+"F0.wireOp",EDGE,"E7.28.4"),sQuery(id+"F0.wireOp",EDGE,"E7.28.5"),sQuery(id+"F0.wireOp",EDGE,"E7.29.0"),sQuery(id+"F0.wireOp",EDGE,"E7.29.1"),sQuery(id+"F0.wireOp",EDGE,"E7.29.2"),sQuery(id+"F0.wireOp",EDGE,"E7.29.3"),sQuery(id+"F0.wireOp",EDGE,"E7.29.4"),sQuery(id+"F0.wireOp",EDGE,"E7.29.5"),sQuery(id+"F0.wireOp",EDGE,"E7.30.0"),sQuery(id+"F0.wireOp",EDGE,"E7.30.1"),sQuery(id+"F0.wireOp",EDGE,"E7.30.2"),sQuery(id+"F0.wireOp",EDGE,"E7.30.3"),sQuery(id+"F0.wireOp",EDGE,"E7.30.4"),sQuery(id+"F0.wireOp",EDGE,"E7.30.5"),sQuery(id+"F0.wireOp",EDGE,"E7.31.0"),sQuery(id+"F0.wireOp",EDGE,"E7.31.1"),sQuery(id+"F0.wireOp",EDGE,"E7.31.2"),sQuery(id+"F0.wireOp",EDGE,"E7.31.3"),sQuery(id+"F0.wireOp",EDGE,"E7.31.4"),sQuery(id+"F0.wireOp",EDGE,"E7.31.5"),sQuery(id+"F0.wireOp",EDGE,"E7.32.0"),sQuery(id+"F0.wireOp",EDGE,"E7.32.1"),sQuery(id+"F0.wireOp",EDGE,"E7.32.2"),sQuery(id+"F0.wireOp",EDGE,"E7.32.3"),sQuery(id+"F0.wireOp",EDGE,"E7.32.4"),sQuery(id+"F0.wireOp",EDGE,"E7.32.5"),sQuery(id+"F0.wireOp",EDGE,"E7.33.0"),sQuery(id+"F0.wireOp",EDGE,"E7.33.1"),sQuery(id+"F0.wireOp",EDGE,"E7.33.2"),sQuery(id+"F0.wireOp",EDGE,"E7.33.3"),sQuery(id+"F0.wireOp",EDGE,"E7.33.4"),sQuery(id+"F0.wireOp",EDGE,"E7.33.5"),sQuery(id+"F0.wireOp",EDGE,"E7.34.0"),sQuery(id+"F0.wireOp",EDGE,"E7.34.1"),sQuery(id+"F0.wireOp",EDGE,"E7.34.2"),sQuery(id+"F0.wireOp",EDGE,"E7.34.3"),sQuery(id+"F0.wireOp",EDGE,"E7.34.4"),sQuery(id+"F0.wireOp",EDGE,"E7.34.5"),sQuery(id+"F0.wireOp",EDGE,"E7.35.0"),sQuery(id+"F0.wireOp",EDGE,"E7.35.1"),sQuery(id+"F0.wireOp",EDGE,"E7.35.2"),sQuery(id+"F0.wireOp",EDGE,"E7.35.3"),sQuery(id+"F0.wireOp",EDGE,"E7.35.4"),sQuery(id+"F0.wireOp",EDGE,"E7.35.5"),sQuery(id+"F0.wireOp",EDGE,"E8.trimOffspring"),sQuery(id+"F0.wireOp",EDGE,"E9.trimOffspring"),sQuery(id+"F0.wireOp",EDGE,"E10.trimOffspring"),sQuery(id+"F0.wireOp",EDGE,"E11.trimOffspring"),sQuery(id+"F0.wireOp",EDGE,"E12.trimOffspring"),sQuery(id+"F0.wireOp",EDGE,"E13.trimOffspring"),sQuery(id+"F0.wireOp",EDGE,"E14.trimOffspring"),sQuery(id+"F0.wireOp",EDGE,"E15.trimOffspring"),sQuery(id+"F0.wireOp",EDGE,"E16.trimOffspring"),sQuery(id+"F0.wireOp",EDGE,"E17.trimOffspring"),sQuery(id+"F0.wireOp",EDGE,"E18.trimOffspring"),sQuery(id+"F0.wireOp",EDGE,"E19.trimOffspring"),sQuery(id+"F0.wireOp",EDGE,"E20.trimOffspring"),sQuery(id+"F0.wireOp",EDGE,"E21.trimOffspring"),sQuery(id+"F0.wireOp",EDGE,"E22.trimOffspring"),sQuery(id+"F0.wireOp",EDGE,"E23.trimOffspring"),sQuery(id+"F0.wireOp",EDGE,"E24.trimOffspring"),sQuery(id+"F0.wireOp",EDGE,"E25.trimOffspring"),sQuery(id+"F0.wireOp",EDGE,"E26.trimOffspring"),sQuery(id+"F0.wireOp",EDGE,"E27.trimOffspring"),sQuery(id+"F0.wireOp",EDGE,"E28.trimOffspring"),sQuery(id+"F0.wireOp",EDGE,"E29.trimOffspring"),sQuery(id+"F0.wireOp",EDGE,"E30.trimOffspring"),sQuery(id+"F0.wireOp",EDGE,"E31.trimOffspring"),sQuery(id+"F0.wireOp",EDGE,"E32.trimOffspring"),sQuery(id+"F0.wireOp",EDGE,"E33.trimOffspring"),sQuery(id+"F0.wireOp",EDGE,"E34.trimOffspring"),sQuery(id+"F0.wireOp",EDGE,"E35.trimOffspring"),sQuery(id+"F0.wireOp",EDGE,"E36.trimOffspring"),sQuery(id+"F0.wireOp",EDGE,"E37.trimOffspring"),sQuery(id+"F0.wireOp",EDGE,"E38.trimOffspring"),sQuery(id+"F0.wireOp",EDGE,"E39.trimOffspring"),sQuery(id+"F0.wireOp",EDGE,"E40.trimOffspring"),sQuery(id+"F0.wireOp",EDGE,"E41.trimOffspring"),sQuery(id+"F0.wireOp",EDGE,"E42.trimOffspring")])],"isStart":true});
            var sketch = newSketch(context, id + "F2", { "sketchPlane" : qUnion([Q0])});
            skCircle(sketch, "E43", {"center": v(0, 0) * mm, "radius": 11.43 * mm});
            skSolve(sketch);
        }
        {
            var Q0;
            Q0=makeQuery(id+"F2.imprint","IMPRINT",FACE,{"disambiguationData":[TD([[makeQuery(id+"F2.imprint","IMPRINT",EDGE,{"derivedFrom":sQuery(id+"F2.wireOp",EDGE,"E43")}),1.0]])]});
            extrude(context, id + "F3", {"entities" : qUnion([Q0]), "operationType" : NewBodyOperationType.ADD, "depth" : 7.37 * mm});
        }
        {
            var Q0;
            Q0=makeQuery(id+"F3.opExtrude","CAP_FACE",FACE,{"disambiguationData":[OSD([sQuery(id+"F2.wireOp",EDGE,"E43")])],"isStart":false});
            var sketch = newSketch(context, id + "F4", { "sketchPlane" : qUnion([Q0])});
            skCircle(sketch, "E44", {"center": v(0, 0) * mm, "radius": 5.59 * mm});
            skCircle(sketch, "E45.cCircle", {"center": v(0, 0) * mm, "radius": 5.59 * mm, "construction": true});
            skLineSegment(sketch, "E45.0", {"start": v(5.64, -3.13) * mm, "end": v(0.1, -6.45) * mm});
            skLineSegment(sketch, "E45.1", {"start": v(0.1, -6.45) * mm, "end": v(-5.53, -3.32) * mm});
            skLineSegment(sketch, "E45.2", {"start": v(-5.53, -3.32) * mm, "end": v(-5.64, 3.13) * mm});
            skLineSegment(sketch, "E45.3", {"start": v(-5.64, 3.13) * mm, "end": v(-0.1, 6.45) * mm});
            skLineSegment(sketch, "E45.4", {"start": v(-0.1, 6.45) * mm, "end": v(5.53, 3.32) * mm});
            skLineSegment(sketch, "E45.5", {"start": v(5.53, 3.32) * mm, "end": v(5.64, -3.13) * mm});
            skPoint(sketch, "E45.0.midPoint", {"position": v(2.88, -4.8) * mm});
            skSolve(sketch);
        }
        {
            var Q0;
            {var subQ0=sQuery(id+"F4.wireOp",EDGE,"E44");var subQ3=makeQuery(id+"F4.imprint","INTERSECT",VERTEX,{"derivedFrom":[subQ0,sQuery(id+"F4.wireOp",EDGE,"E45.4")]});Q0=makeQuery(id+"F4.imprint","IMPRINT",FACE,{"disambiguationData":[TD([[makeQuery(id+"F4.imprint","IMPRINT",EDGE,{"disambiguationData":[TD([[subQ3,1.0]])],"derivedFrom":subQ0}),1.0]])]});}
            var Q1;
            {var subQ0=sQuery(id+"F4.wireOp",EDGE,"E45.4");var subQ1=sQuery(id+"F4.wireOp",EDGE,"E44");var subQ2=makeQuery(id+"F4.imprint","INTERSECT",VERTEX,{"derivedFrom":[subQ1,subQ0]});Q1=makeQuery(id+"F4.imprint","IMPRINT",FACE,{"disambiguationData":[TD([[makeQuery(id+"F4.imprint","IMPRINT",EDGE,{"disambiguationData":[TD([[subQ2,-1.0]])],"derivedFrom":subQ1}),-1.0]])]});}
            var Q2;
            {var subQ0=sQuery(id+"F4.wireOp",EDGE,"E45.3");var subQ1=sQuery(id+"F4.wireOp",EDGE,"E44");var subQ2=makeQuery(id+"F4.imprint","INTERSECT",VERTEX,{"derivedFrom":[subQ1,subQ0]});Q2=makeQuery(id+"F4.imprint","IMPRINT",FACE,{"disambiguationData":[TD([[makeQuery(id+"F4.imprint","IMPRINT",EDGE,{"disambiguationData":[TD([[subQ2,-1.0]])],"derivedFrom":subQ1}),-1.0]])]});}
            var Q3;
            {var subQ0=sQuery(id+"F4.wireOp",EDGE,"E45.4");var subQ1=sQuery(id+"F4.wireOp",EDGE,"E44");var subQ2=makeQuery(id+"F4.imprint","INTERSECT",VERTEX,{"derivedFrom":[subQ1,subQ0]});Q3=makeQuery(id+"F4.imprint","IMPRINT",FACE,{"disambiguationData":[TD([[makeQuery(id+"F4.imprint","IMPRINT",EDGE,{"disambiguationData":[TD([[subQ2,1.0]])],"derivedFrom":subQ1}),-1.0]])]});}
            var Q4;
            {var subQ0=sQuery(id+"F4.wireOp",EDGE,"E45.5");var subQ1=sQuery(id+"F4.wireOp",EDGE,"E44");var subQ2=makeQuery(id+"F4.imprint","INTERSECT",VERTEX,{"derivedFrom":[subQ1,subQ0]});Q4=makeQuery(id+"F4.imprint","IMPRINT",FACE,{"disambiguationData":[TD([[makeQuery(id+"F4.imprint","IMPRINT",EDGE,{"disambiguationData":[TD([[subQ2,1.0]])],"derivedFrom":subQ1}),-1.0]])]});}
            var Q5;
            {var subQ0=sQuery(id+"F4.wireOp",EDGE,"E45.1");var subQ1=sQuery(id+"F4.wireOp",EDGE,"E44");var subQ2=makeQuery(id+"F4.imprint","INTERSECT",VERTEX,{"derivedFrom":[subQ1,subQ0]});Q5=makeQuery(id+"F4.imprint","IMPRINT",FACE,{"disambiguationData":[TD([[makeQuery(id+"F4.imprint","IMPRINT",EDGE,{"disambiguationData":[TD([[subQ2,-1.0]])],"derivedFrom":subQ1}),-1.0]])]});}
            var Q6;
            {var subQ0=sQuery(id+"F4.wireOp",EDGE,"E45.2");var subQ1=sQuery(id+"F4.wireOp",EDGE,"E44");var subQ2=makeQuery(id+"F4.imprint","INTERSECT",VERTEX,{"derivedFrom":[subQ1,subQ0]});Q6=makeQuery(id+"F4.imprint","IMPRINT",FACE,{"disambiguationData":[TD([[makeQuery(id+"F4.imprint","IMPRINT",EDGE,{"disambiguationData":[TD([[subQ2,-1.0]])],"derivedFrom":subQ1}),-1.0]])]});}
            extrude(context, id + "F5", {"entities" : qUnion([Q0, Q1, Q2, Q3, Q4, Q5, Q6]), "operationType" : NewBodyOperationType.REMOVE, "oppositeDirection" : true, "depth" : 25.4 * mm});
        }
    });
